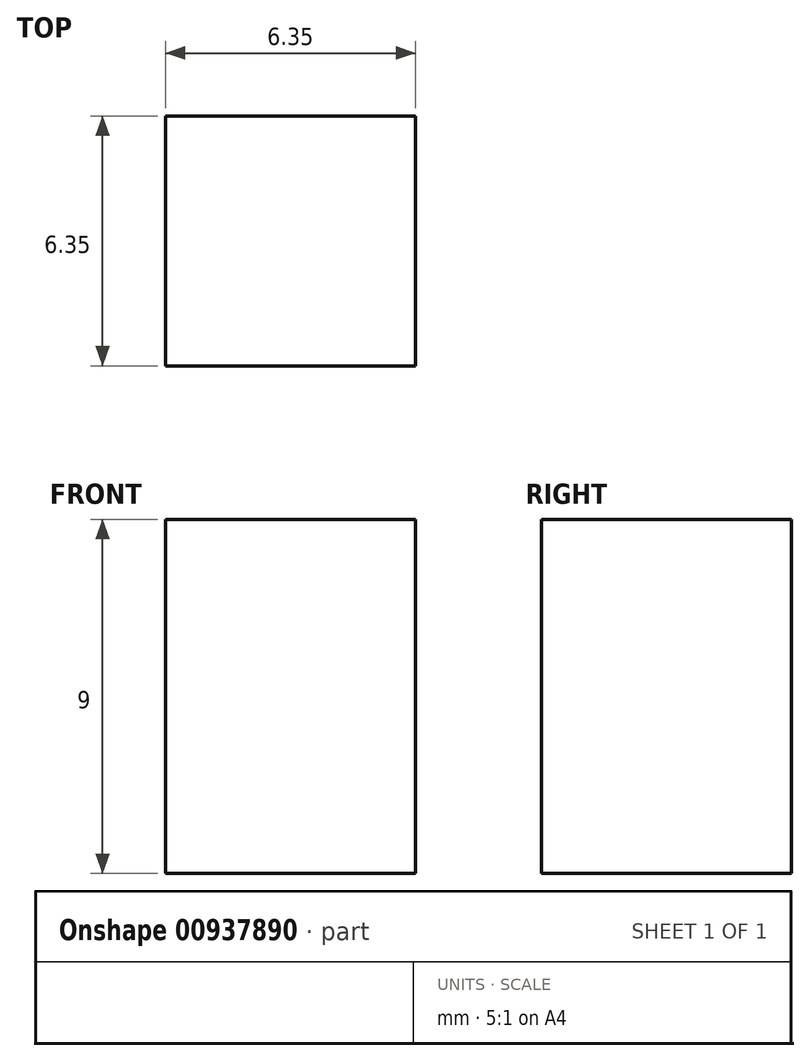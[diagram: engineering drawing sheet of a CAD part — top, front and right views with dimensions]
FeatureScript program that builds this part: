
annotation { "Feature Type Name" : "Feature", "Feature Type Description" : "" }
export const myFeature = defineFeature(function(context is Context, id is Id, definition is map)
    precondition{}
    {
        {
            var Q0;
            Q0=qCreatedBy(makeId("Top.planeOp"),FACE);
            var sketch = newSketch(context, id + "F0", { "sketchPlane" : qUnion([Q0])});
            skLineSegment(sketch, "E0.bottom", {"start": v(-45.9, 40.03) * mm, "end": v(-39.56, 40.03) * mm});
            skLineSegment(sketch, "E0.top", {"start": v(-45.9, 33.68) * mm, "end": v(-39.56, 33.68) * mm});
            skLineSegment(sketch, "E0.left", {"start": v(-45.9, 40.03) * mm, "end": v(-45.9, 33.68) * mm});
            skLineSegment(sketch, "E0.right", {"start": v(-39.56, 40.03) * mm, "end": v(-39.56, 33.68) * mm});
            skSolve(sketch);
        }
        {
            var Q0;
            Q0=makeQuery(id+"F0.imprint","IMPRINT",FACE,{"disambiguationData":[TD([[makeQuery(id+"F0.imprint","IMPRINT",EDGE,{"derivedFrom":sQuery(id+"F0.wireOp",EDGE,"E0.bottom")}),-1.0]])]});
            extrude(context, id + "F1", {"entities" : qUnion([Q0]), "depth" : 9 * mm, "offsetDistance" : 25.4 * mm});
        }
    });
